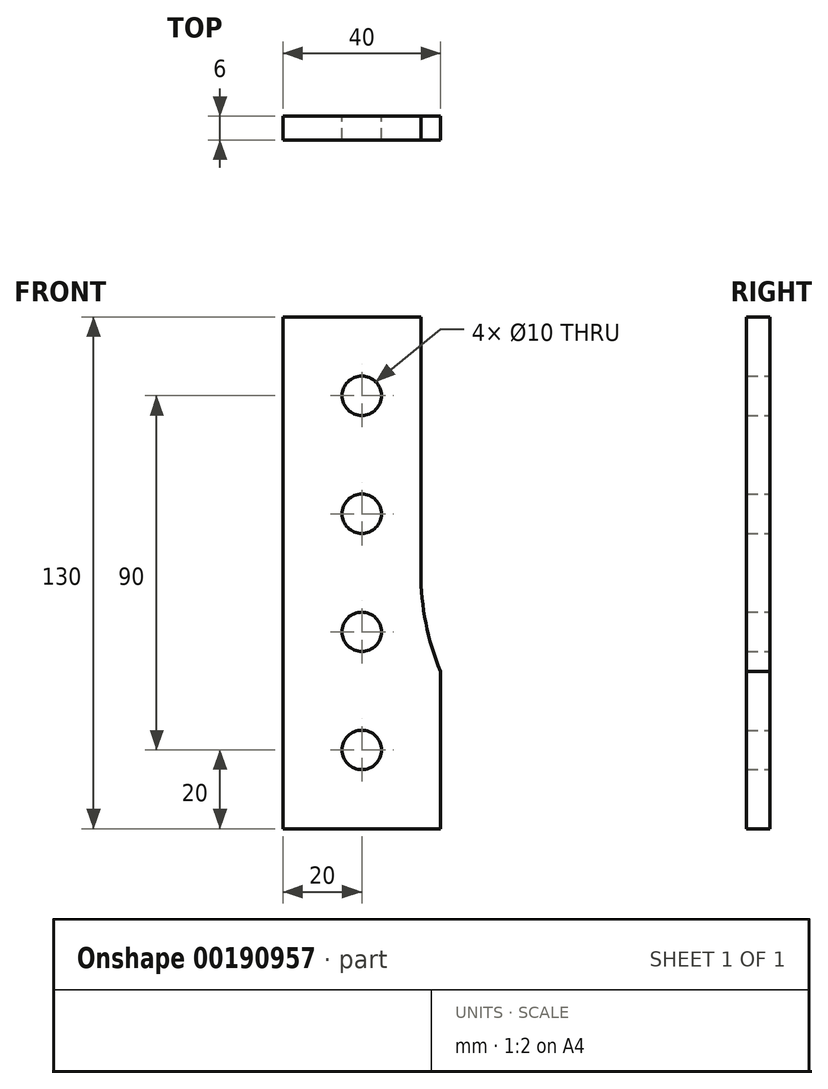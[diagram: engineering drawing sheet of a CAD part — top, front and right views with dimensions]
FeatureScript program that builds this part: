
annotation { "Feature Type Name" : "Feature", "Feature Type Description" : "" }
export const myFeature = defineFeature(function(context is Context, id is Id, definition is map)
    precondition{}
    {
        {
            var Q0;
            Q0=qCreatedBy(makeId("Front.planeOp"),FACE);
            var sketch = newSketch(context, id + "F0", { "sketchPlane" : qUnion([Q0])});
            skLineSegment(sketch, "E0.bottom", {"start": v(0, 0) * mm, "end": v(40, 0) * mm});
            skLineSegment(sketch, "E0.top", {"start": v(0, 130) * mm, "end": v(40, 130) * mm});
            skLineSegment(sketch, "E0.left", {"start": v(0, 0) * mm, "end": v(0, 130) * mm});
            skLineSegment(sketch, "E0.right", {"start": v(40, 0) * mm, "end": v(40, 130) * mm});
            skArc(sketch, "E1", {"start": v(40, 40) * mm, "mid": v(35, 65) * mm, "end": v(40, 90) * mm});
            skCircle(sketch, "E2", {"center": v(20, 110) * mm, "radius": 5 * mm});
            skCircle(sketch, "E3", {"center": v(20, 80) * mm, "radius": 5 * mm});
            skCircle(sketch, "E4", {"center": v(20, 50) * mm, "radius": 5 * mm});
            skCircle(sketch, "E5", {"center": v(20, 20) * mm, "radius": 5 * mm});
            skLineSegment(sketch, "E6.bottom", {"start": v(40, 130) * mm, "end": v(35, 130) * mm});
            skLineSegment(sketch, "E6.top", {"start": v(40, 65) * mm, "end": v(35, 65) * mm});
            skLineSegment(sketch, "E6.left", {"start": v(40, 130) * mm, "end": v(40, 65) * mm});
            skLineSegment(sketch, "E6.right", {"start": v(35, 130) * mm, "end": v(35, 65) * mm});
            skSolve(sketch);
        }
        {
            var Q0;
            {var subQ1=sQuery(id+"F0.wireOp",EDGE,"E0.bottom");Q0=makeQuery(id+"F0.imprint","IMPRINT",FACE,{"disambiguationData":[TD([[makeQuery(id+"F0.imprint","IMPRINT",EDGE,{"derivedFrom":subQ1}),1.0]])]});}
            extrude(context, id + "F1", {"entities" : qUnion([Q0]), "depth" : 6 * mm});
        }
    });
